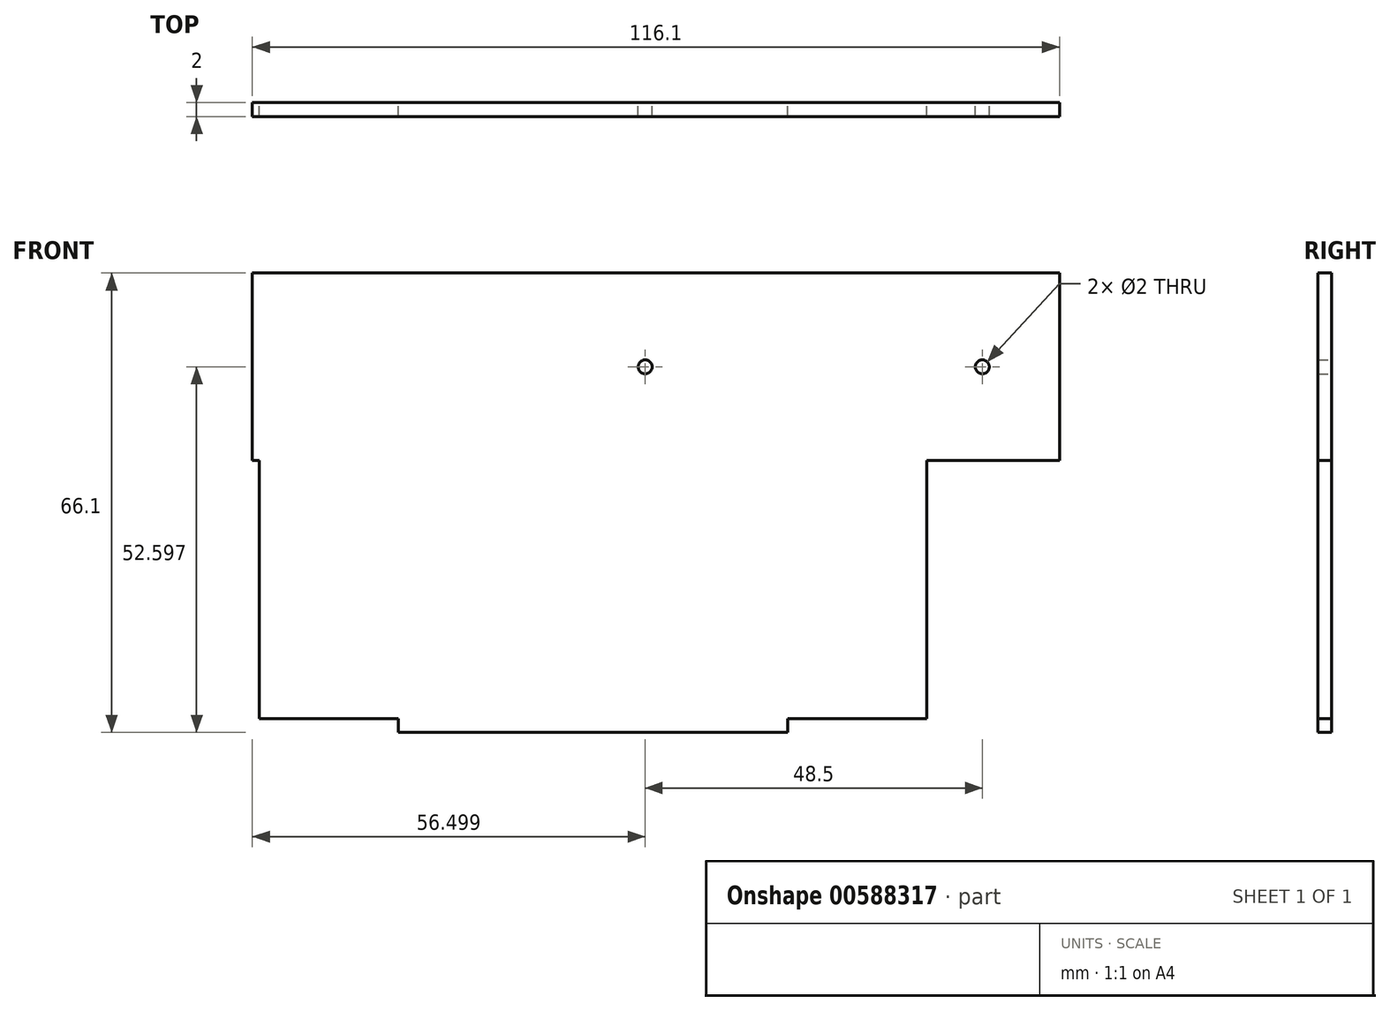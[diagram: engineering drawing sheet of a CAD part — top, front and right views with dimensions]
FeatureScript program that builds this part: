
annotation { "Feature Type Name" : "Feature", "Feature Type Description" : "" }
export const myFeature = defineFeature(function(context is Context, id is Id, definition is map)
    precondition{}
    {
        {
            var Q0;
            Q0=qCreatedBy(makeId("Front.planeOp"),FACE);
            var sketch = newSketch(context, id + "F0", { "sketchPlane" : qUnion([Q0])});
            skLineSegment(sketch, "E0.left", {"start": v(-10.01, 20.87) * mm, "end": v(-10.01, -14.77) * mm});
            skLineSegment(sketch, "E0.right", {"start": v(85.99, 15.87) * mm, "end": v(85.99, -14.77) * mm});
            skLineSegment(sketch, "E1", {"start": v(-10.01, 20.87) * mm, "end": v(-11.01, 20.87) * mm});
            skLineSegment(sketch, "E2", {"start": v(-11.01, 20.87) * mm, "end": v(-11.01, 15.87) * mm});
            skLineSegment(sketch, "E3", {"start": v(-11.01, 15.87) * mm, "end": v(-10.01, 15.87) * mm});
            skLineSegment(sketch, "E4", {"start": v(85.99, 20.87) * mm, "end": v(88.99, 20.87) * mm});
            skLineSegment(sketch, "E5", {"start": v(88.99, 20.87) * mm, "end": v(98.99, 20.87) * mm});
            skLineSegment(sketch, "E6", {"start": v(98.99, 15.87) * mm, "end": v(85.99, 15.87) * mm});
            skLineSegment(sketch, "E7", {"start": v(85.99, 15.87) * mm, "end": v(85.99, -21.23) * mm});
            skLineSegment(sketch, "E8", {"start": v(85.99, -21.23) * mm, "end": v(65.99, -21.23) * mm});
            skLineSegment(sketch, "E9", {"start": v(-10.01, -21.23) * mm, "end": v(-10.01, -14.77) * mm});
            skLineSegment(sketch, "E10", {"start": v(-10.01, -21.23) * mm, "end": v(9.99, -21.23) * mm});
            skLineSegment(sketch, "E11", {"start": v(9.99, -21.23) * mm, "end": v(9.99, -23.23) * mm});
            skLineSegment(sketch, "E12", {"start": v(65.99, -21.23) * mm, "end": v(65.99, -23.23) * mm});
            skLineSegment(sketch, "E13", {"start": v(65.99, -23.23) * mm, "end": v(9.99, -23.23) * mm});
            skLineSegment(sketch, "E14", {"start": v(98.99, 42.87) * mm, "end": v(-10.01, 42.87) * mm});
            skLineSegment(sketch, "E15", {"start": v(-11.01, 20.87) * mm, "end": v(-11.01, 42.87) * mm});
            skLineSegment(sketch, "E16", {"start": v(-11.01, 42.87) * mm, "end": v(-10.01, 42.87) * mm});
            skLineSegment(sketch, "E17.trimOffspring", {"start": v(9.99, -21.23) * mm, "end": v(-10.01, -21.23) * mm});
            skLineSegment(sketch, "E18", {"start": v(9.99, -23.23) * mm, "end": v(37.99, -23.23) * mm});
            skLineSegment(sketch, "E19", {"start": v(37.99, 42.87) * mm, "end": v(37.99, 15.87) * mm});
            skLineSegment(sketch, "E20", {"start": v(37.99, 29.37) * mm, "end": v(44.49, 29.37) * mm});
            skCircle(sketch, "E21", {"center": v(45.49, 29.37) * mm, "radius": 1 * mm});
            skLineSegment(sketch, "E22", {"start": v(98.99, 42.87) * mm, "end": v(93.99, 42.87) * mm});
            skLineSegment(sketch, "E23", {"start": v(93.99, 28.37) * mm, "end": v(93.99, 20.87) * mm});
            skPoint(sketch, "E23.endSnap0", {"position": v(93.99, 20.87) * mm});
            skCircle(sketch, "E24", {"center": v(93.99, 29.37) * mm, "radius": 1 * mm});
            skLineSegment(sketch, "E25", {"start": v(98.99, 15.87) * mm, "end": v(103.99, 15.87) * mm});
            skLineSegment(sketch, "E26", {"start": v(103.99, 42.87) * mm, "end": v(98.99, 42.87) * mm});
            skPoint(sketch, "E27.orphan", {"position": v(93.99, 15.87) * mm});
            skLineSegment(sketch, "E28", {"start": v(103.99, 42.87) * mm, "end": v(105.1, 42.87) * mm});
            skLineSegment(sketch, "E29", {"start": v(105.1, 42.87) * mm, "end": v(105.1, 15.87) * mm});
            skLineSegment(sketch, "E30", {"start": v(105.1, 15.87) * mm, "end": v(103.99, 15.87) * mm});
            skSolve(sketch);
        }
        {
            var Q0;
            {var subQ4=sQuery(id+"F0.wireOp",EDGE,"E0.bottom");Q0=makeQuery(id+"F0.imprint","IMPRINT",FACE,{"disambiguationData":[TD([[makeQuery(id+"F0.imprint","IMPRINT",EDGE,{"derivedFrom":subQ4}),-1.0]])]});}
            var Q1;
            Q1=makeQuery(id+"F0.imprint","IMPRINT",FACE,{"disambiguationData":[TD([[makeQuery(id+"F0.imprint","IMPRINT",EDGE,{"derivedFrom":sQuery(id+"F0.wireOp",EDGE,"E8")}),1.0]])]});
            var Q2;
            {var subQ0=sQuery(id+"F0.wireOp",EDGE,"E1");Q2=makeQuery(id+"F0.imprint","IMPRINT",FACE,{"disambiguationData":[TD([[makeQuery(id+"F0.imprint","IMPRINT",EDGE,{"derivedFrom":subQ0}),1.0]])]});}
            var Q3;
            Q3=makeQuery(id+"F0.imprint","IMPRINT",FACE,{"disambiguationData":[TD([[makeQuery(id+"F0.imprint","IMPRINT",EDGE,{"derivedFrom":sQuery(id+"F0.wireOp",EDGE,"E0.right")}),1.0]])]});
            extrude(context, id + "F1", {"entities" : qUnion([Q0, Q1, Q2, Q3]), "depth" : 2 * mm, "offsetDistance" : 25 * mm});
        }
        {
            var Q0;
            {var subQ4=sQuery(id+"F0.wireOp",EDGE,"E1");Q0=makeQuery(id+"F0.imprint","IMPRINT",FACE,{"disambiguationData":[TD([[makeQuery(id+"F0.imprint","IMPRINT",EDGE,{"derivedFrom":subQ4}),-1.0]])]});}
            extrude(context, id + "F2", {"entities" : qUnion([Q0]), "operationType" : NewBodyOperationType.ADD, "depth" : 2 * mm, "offsetDistance" : 25 * mm});
        }
    });
